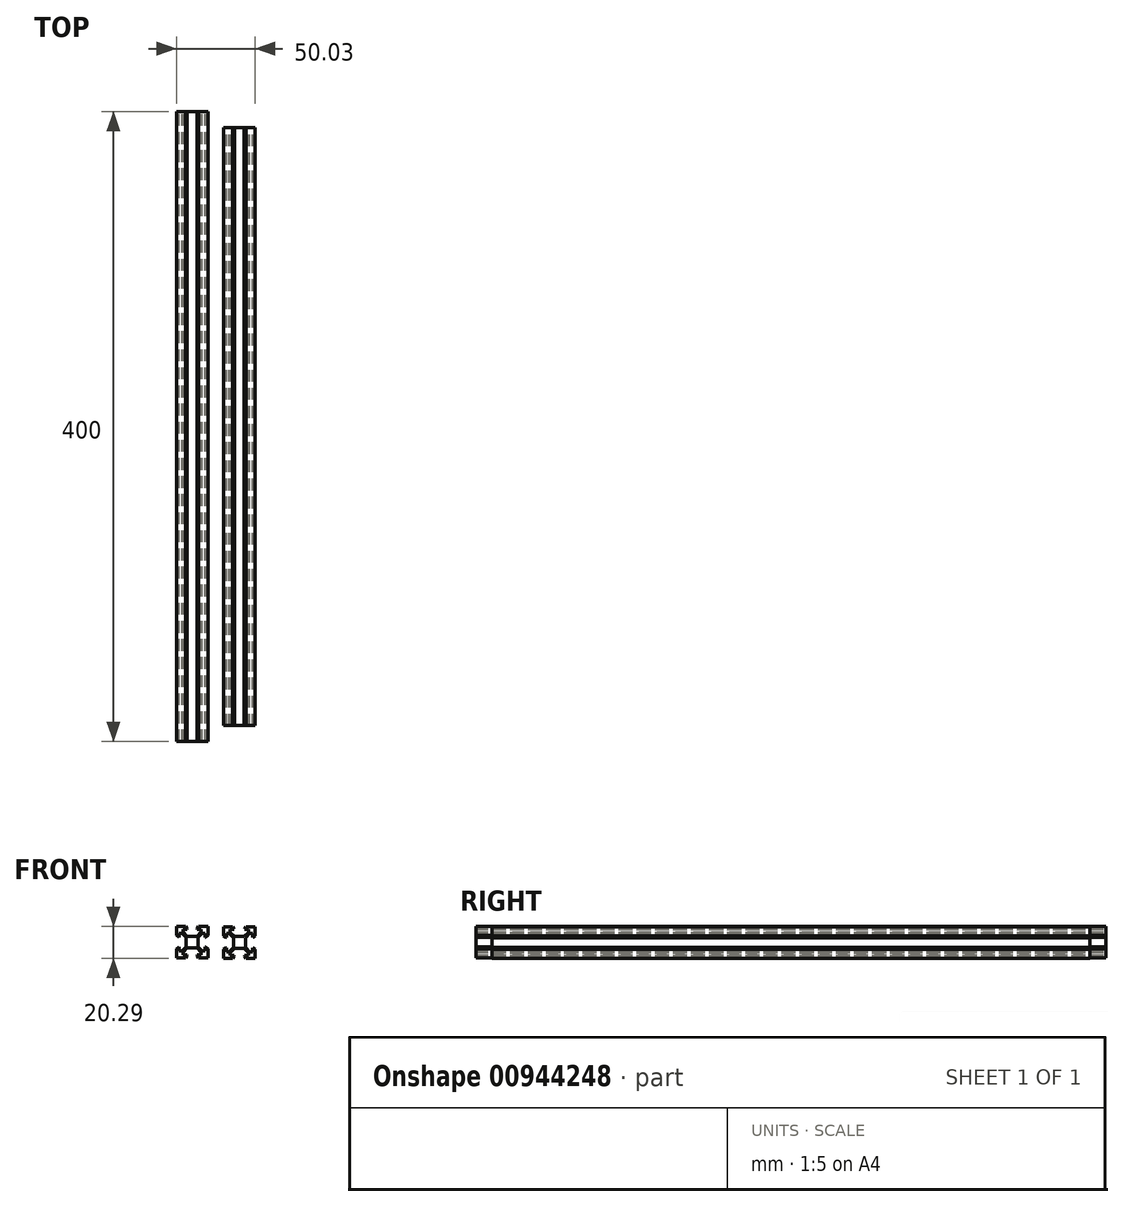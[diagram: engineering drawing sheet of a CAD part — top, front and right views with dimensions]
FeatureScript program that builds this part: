
annotation { "Feature Type Name" : "Feature", "Feature Type Description" : "" }
export const myFeature = defineFeature(function(context is Context, id is Id, definition is map)
    precondition{}
    {
        {
            var Q0;
            Q0=qCreatedBy(makeId("Front.planeOp"),FACE);
            var sketch = newSketch(context, id + "F0", { "sketchPlane" : qUnion([Q0])});
            skLineSegment(sketch, "E0.bottom", {"start": v(10, -10) * mm, "end": v(-10, -10) * mm});
            skLineSegment(sketch, "E0.top", {"start": v(10, 10) * mm, "end": v(-10, 10) * mm});
            skLineSegment(sketch, "E0.left", {"start": v(10, -10) * mm, "end": v(10, 10) * mm});
            skLineSegment(sketch, "E0.right", {"start": v(-10, -10) * mm, "end": v(-10, 10) * mm});
            skPoint(sketch, "E0.middle", {"position": v(0, 0) * mm});
            skLineSegment(sketch, "E1", {"start": v(4.24, 10) * mm, "end": v(3.26, 8.42) * mm});
            skLineSegment(sketch, "E2", {"start": v(3.26, 8.42) * mm, "end": v(3.26, 8.22) * mm});
            skLineSegment(sketch, "E3", {"start": v(3.26, 8.22) * mm, "end": v(5.76, 8.22) * mm});
            skLineSegment(sketch, "E4", {"start": v(5.76, 8.22) * mm, "end": v(5.76, 6.44) * mm});
            skLineSegment(sketch, "E5", {"start": v(5.76, 6.44) * mm, "end": v(3.11, 3.78) * mm});
            skLineSegment(sketch, "E6", {"start": v(3.11, 3.78) * mm, "end": v(0, 3.78) * mm});
            skLineSegment(sketch, "E7", {"start": v(0, 15.87) * mm, "end": v(0, -18.37) * mm, "construction": true});
            skPoint(sketch, "E7.endSnap0", {"position": v(0, -10) * mm});
            skLineSegment(sketch, "E8.MirrorCS", {"start": v(-4.24, 10) * mm, "end": v(-3.26, 8.42) * mm});
            skLineSegment(sketch, "E9.MirrorCS", {"start": v(-3.26, 8.42) * mm, "end": v(-3.26, 8.22) * mm});
            skLineSegment(sketch, "E10.MirrorCS", {"start": v(-3.26, 8.22) * mm, "end": v(-5.76, 8.22) * mm});
            skLineSegment(sketch, "E11.MirrorCS", {"start": v(-5.46, 15.87) * mm, "end": v(-5.46, -18.37) * mm, "construction": true});
            skLineSegment(sketch, "E12.MirrorCS", {"start": v(-5.76, 6.44) * mm, "end": v(-3.11, 3.78) * mm});
            skLineSegment(sketch, "E13.MirrorCS", {"start": v(-3.11, 3.78) * mm, "end": v(0, 3.78) * mm});
            skLineSegment(sketch, "E14.MirrorCS", {"start": v(-5.76, 8.22) * mm, "end": v(-5.76, 6.44) * mm});
            skLineSegment(sketch, "E15.1.0", {"start": v(-3.78, 3.11) * mm, "end": v(-3.78, 0) * mm});
            skLineSegment(sketch, "E15.1.1", {"start": v(-3.78, -3.11) * mm, "end": v(-3.78, 0) * mm});
            skLineSegment(sketch, "E15.1.2", {"start": v(-6.44, -5.76) * mm, "end": v(-3.78, -3.11) * mm});
            skLineSegment(sketch, "E15.1.3", {"start": v(-8.22, 3.26) * mm, "end": v(-8.22, 5.76) * mm});
            skLineSegment(sketch, "E15.1.4", {"start": v(-10, 4.24) * mm, "end": v(-8.42, 3.26) * mm});
            skLineSegment(sketch, "E15.1.5", {"start": v(-8.22, 5.76) * mm, "end": v(-6.44, 5.76) * mm});
            skLineSegment(sketch, "E15.1.6", {"start": v(-10, -4.24) * mm, "end": v(-8.42, -3.26) * mm});
            skLineSegment(sketch, "E15.1.7", {"start": v(-6.44, 5.76) * mm, "end": v(-3.78, 3.11) * mm});
            skLineSegment(sketch, "E15.1.8", {"start": v(-8.22, -5.76) * mm, "end": v(-6.44, -5.76) * mm});
            skLineSegment(sketch, "E15.1.9", {"start": v(-8.22, -3.26) * mm, "end": v(-8.22, -5.76) * mm});
            skLineSegment(sketch, "E15.1.10", {"start": v(-8.42, -3.26) * mm, "end": v(-8.22, -3.26) * mm});
            skLineSegment(sketch, "E15.1.11", {"start": v(-8.42, 3.26) * mm, "end": v(-8.22, 3.26) * mm});
            skLineSegment(sketch, "E15.2.0", {"start": v(-3.11, -3.78) * mm, "end": v(0, -3.78) * mm});
            skLineSegment(sketch, "E15.2.1", {"start": v(3.11, -3.78) * mm, "end": v(0, -3.78) * mm});
            skLineSegment(sketch, "E15.2.2", {"start": v(5.76, -6.44) * mm, "end": v(3.11, -3.78) * mm});
            skLineSegment(sketch, "E15.2.3", {"start": v(-3.26, -8.22) * mm, "end": v(-5.76, -8.22) * mm});
            skLineSegment(sketch, "E15.2.4", {"start": v(-4.24, -10) * mm, "end": v(-3.26, -8.42) * mm});
            skLineSegment(sketch, "E15.2.5", {"start": v(-5.76, -8.22) * mm, "end": v(-5.76, -6.44) * mm});
            skLineSegment(sketch, "E15.2.6", {"start": v(4.24, -10) * mm, "end": v(3.26, -8.42) * mm});
            skLineSegment(sketch, "E15.2.7", {"start": v(-5.76, -6.44) * mm, "end": v(-3.11, -3.78) * mm});
            skLineSegment(sketch, "E15.2.8", {"start": v(5.76, -8.22) * mm, "end": v(5.76, -6.44) * mm});
            skLineSegment(sketch, "E15.2.9", {"start": v(3.26, -8.22) * mm, "end": v(5.76, -8.22) * mm});
            skLineSegment(sketch, "E15.2.10", {"start": v(3.26, -8.42) * mm, "end": v(3.26, -8.22) * mm});
            skLineSegment(sketch, "E15.2.11", {"start": v(-3.26, -8.42) * mm, "end": v(-3.26, -8.22) * mm});
            skLineSegment(sketch, "E15.3.0", {"start": v(3.78, -3.11) * mm, "end": v(3.78, 0) * mm});
            skLineSegment(sketch, "E15.3.1", {"start": v(3.78, 3.11) * mm, "end": v(3.78, 0) * mm});
            skLineSegment(sketch, "E15.3.2", {"start": v(6.44, 5.76) * mm, "end": v(3.78, 3.11) * mm});
            skLineSegment(sketch, "E15.3.3", {"start": v(8.22, -3.26) * mm, "end": v(8.22, -5.76) * mm});
            skLineSegment(sketch, "E15.3.4", {"start": v(10, -4.24) * mm, "end": v(8.42, -3.26) * mm});
            skLineSegment(sketch, "E15.3.5", {"start": v(8.22, -5.76) * mm, "end": v(6.44, -5.76) * mm});
            skLineSegment(sketch, "E15.3.6", {"start": v(10, 4.24) * mm, "end": v(8.42, 3.26) * mm});
            skLineSegment(sketch, "E15.3.7", {"start": v(6.44, -5.76) * mm, "end": v(3.78, -3.11) * mm});
            skLineSegment(sketch, "E15.3.8", {"start": v(8.22, 5.76) * mm, "end": v(6.44, 5.76) * mm});
            skLineSegment(sketch, "E15.3.9", {"start": v(8.22, 3.26) * mm, "end": v(8.22, 5.76) * mm});
            skLineSegment(sketch, "E15.3.10", {"start": v(8.42, 3.26) * mm, "end": v(8.22, 3.26) * mm});
            skLineSegment(sketch, "E15.3.11", {"start": v(8.42, -3.26) * mm, "end": v(8.22, -3.26) * mm});
            skSolve(sketch);
        }
        {
            var Q0;
            {var subQ15=sQuery(id+"F0.wireOp",EDGE,"E1");Q0=makeQuery(id+"F0.imprint","IMPRINT",FACE,{"disambiguationData":[TD([[makeQuery(id+"F0.imprint","IMPRINT",EDGE,{"derivedFrom":subQ15}),1.0]])]});}
            extrude(context, id + "F1", {"entities" : qUnion([Q0]), "depth" : 380 * mm, "symmetric" : true});
        }
        {
            var Q0;
            Q0=makeQuery(id+"F1.opExtrude","SWEPT_BODY",BODY,{"disambiguationData":[OSD([sQuery(id+"F0.wireOp",EDGE,"E0.bottom"),sQuery(id+"F0.wireOp",EDGE,"E0.top"),sQuery(id+"F0.wireOp",EDGE,"E0.left"),sQuery(id+"F0.wireOp",EDGE,"E0.right"),sQuery(id+"F0.wireOp",EDGE,"E1"),sQuery(id+"F0.wireOp",EDGE,"E2"),sQuery(id+"F0.wireOp",EDGE,"E3"),sQuery(id+"F0.wireOp",EDGE,"E4"),sQuery(id+"F0.wireOp",EDGE,"E5"),sQuery(id+"F0.wireOp",EDGE,"E6"),sQuery(id+"F0.wireOp",EDGE,"E8.MirrorCS"),sQuery(id+"F0.wireOp",EDGE,"E9.MirrorCS"),sQuery(id+"F0.wireOp",EDGE,"E10.MirrorCS"),sQuery(id+"F0.wireOp",EDGE,"E12.MirrorCS"),sQuery(id+"F0.wireOp",EDGE,"E13.MirrorCS"),sQuery(id+"F0.wireOp",EDGE,"E14.MirrorCS"),sQuery(id+"F0.wireOp",EDGE,"E15.1.0"),sQuery(id+"F0.wireOp",EDGE,"E15.1.1"),sQuery(id+"F0.wireOp",EDGE,"E15.1.2"),sQuery(id+"F0.wireOp",EDGE,"E15.1.3"),sQuery(id+"F0.wireOp",EDGE,"E15.1.4"),sQuery(id+"F0.wireOp",EDGE,"E15.1.5"),sQuery(id+"F0.wireOp",EDGE,"E15.1.6"),sQuery(id+"F0.wireOp",EDGE,"E15.1.7"),sQuery(id+"F0.wireOp",EDGE,"E15.1.8"),sQuery(id+"F0.wireOp",EDGE,"E15.1.9"),sQuery(id+"F0.wireOp",EDGE,"E15.1.10"),sQuery(id+"F0.wireOp",EDGE,"E15.1.11"),sQuery(id+"F0.wireOp",EDGE,"E15.2.0"),sQuery(id+"F0.wireOp",EDGE,"E15.2.1"),sQuery(id+"F0.wireOp",EDGE,"E15.2.2"),sQuery(id+"F0.wireOp",EDGE,"E15.2.3"),sQuery(id+"F0.wireOp",EDGE,"E15.2.4"),sQuery(id+"F0.wireOp",EDGE,"E15.2.5"),sQuery(id+"F0.wireOp",EDGE,"E15.2.6"),sQuery(id+"F0.wireOp",EDGE,"E15.2.7"),sQuery(id+"F0.wireOp",EDGE,"E15.2.8"),sQuery(id+"F0.wireOp",EDGE,"E15.2.9"),sQuery(id+"F0.wireOp",EDGE,"E15.2.10"),sQuery(id+"F0.wireOp",EDGE,"E15.2.11"),sQuery(id+"F0.wireOp",EDGE,"E15.3.0"),sQuery(id+"F0.wireOp",EDGE,"E15.3.1"),sQuery(id+"F0.wireOp",EDGE,"E15.3.2"),sQuery(id+"F0.wireOp",EDGE,"E15.3.3"),sQuery(id+"F0.wireOp",EDGE,"E15.3.4"),sQuery(id+"F0.wireOp",EDGE,"E15.3.5"),sQuery(id+"F0.wireOp",EDGE,"E15.3.6"),sQuery(id+"F0.wireOp",EDGE,"E15.3.7"),sQuery(id+"F0.wireOp",EDGE,"E15.3.8"),sQuery(id+"F0.wireOp",EDGE,"E15.3.9"),sQuery(id+"F0.wireOp",EDGE,"E15.3.10"),sQuery(id+"F0.wireOp",EDGE,"E15.3.11")])]});
            transform(context, id + "F2", {"entities" : qUnion([Q0]), "transformType" : TransformType.COPY});
        }
        {
            var Q0;
            Q0=makeQuery(id+"F2.opPattern","COPY",BODY,{"derivedFrom":makeQuery(id+"F1.opExtrude","SWEPT_BODY",BODY,{"disambiguationData":[OSD([sQuery(id+"F0.wireOp",EDGE,"E0.bottom"),sQuery(id+"F0.wireOp",EDGE,"E0.top"),sQuery(id+"F0.wireOp",EDGE,"E0.left"),sQuery(id+"F0.wireOp",EDGE,"E0.right"),sQuery(id+"F0.wireOp",EDGE,"E1"),sQuery(id+"F0.wireOp",EDGE,"E2"),sQuery(id+"F0.wireOp",EDGE,"E3"),sQuery(id+"F0.wireOp",EDGE,"E4"),sQuery(id+"F0.wireOp",EDGE,"E5"),sQuery(id+"F0.wireOp",EDGE,"E6"),sQuery(id+"F0.wireOp",EDGE,"E8.MirrorCS"),sQuery(id+"F0.wireOp",EDGE,"E9.MirrorCS"),sQuery(id+"F0.wireOp",EDGE,"E10.MirrorCS"),sQuery(id+"F0.wireOp",EDGE,"E12.MirrorCS"),sQuery(id+"F0.wireOp",EDGE,"E13.MirrorCS"),sQuery(id+"F0.wireOp",EDGE,"E14.MirrorCS"),sQuery(id+"F0.wireOp",EDGE,"E15.1.0"),sQuery(id+"F0.wireOp",EDGE,"E15.1.1"),sQuery(id+"F0.wireOp",EDGE,"E15.1.2"),sQuery(id+"F0.wireOp",EDGE,"E15.1.3"),sQuery(id+"F0.wireOp",EDGE,"E15.1.4"),sQuery(id+"F0.wireOp",EDGE,"E15.1.5"),sQuery(id+"F0.wireOp",EDGE,"E15.1.6"),sQuery(id+"F0.wireOp",EDGE,"E15.1.7"),sQuery(id+"F0.wireOp",EDGE,"E15.1.8"),sQuery(id+"F0.wireOp",EDGE,"E15.1.9"),sQuery(id+"F0.wireOp",EDGE,"E15.1.10"),sQuery(id+"F0.wireOp",EDGE,"E15.1.11"),sQuery(id+"F0.wireOp",EDGE,"E15.2.0"),sQuery(id+"F0.wireOp",EDGE,"E15.2.1"),sQuery(id+"F0.wireOp",EDGE,"E15.2.2"),sQuery(id+"F0.wireOp",EDGE,"E15.2.3"),sQuery(id+"F0.wireOp",EDGE,"E15.2.4"),sQuery(id+"F0.wireOp",EDGE,"E15.2.5"),sQuery(id+"F0.wireOp",EDGE,"E15.2.6"),sQuery(id+"F0.wireOp",EDGE,"E15.2.7"),sQuery(id+"F0.wireOp",EDGE,"E15.2.8"),sQuery(id+"F0.wireOp",EDGE,"E15.2.9"),sQuery(id+"F0.wireOp",EDGE,"E15.2.10"),sQuery(id+"F0.wireOp",EDGE,"E15.2.11"),sQuery(id+"F0.wireOp",EDGE,"E15.3.0"),sQuery(id+"F0.wireOp",EDGE,"E15.3.1"),sQuery(id+"F0.wireOp",EDGE,"E15.3.2"),sQuery(id+"F0.wireOp",EDGE,"E15.3.3"),sQuery(id+"F0.wireOp",EDGE,"E15.3.4"),sQuery(id+"F0.wireOp",EDGE,"E15.3.5"),sQuery(id+"F0.wireOp",EDGE,"E15.3.6"),sQuery(id+"F0.wireOp",EDGE,"E15.3.7"),sQuery(id+"F0.wireOp",EDGE,"E15.3.8"),sQuery(id+"F0.wireOp",EDGE,"E15.3.9"),sQuery(id+"F0.wireOp",EDGE,"E15.3.10"),sQuery(id+"F0.wireOp",EDGE,"E15.3.11")])]}),"instanceName":"1"});
            deleteBodies(context, id + "F3", {"entities" : qUnion([Q0])});
        }
        {
            var Q0;
            Q0=makeQuery(id+"F1.opExtrude","SWEPT_BODY",BODY,{"disambiguationData":[OSD([sQuery(id+"F0.wireOp",EDGE,"E0.bottom"),sQuery(id+"F0.wireOp",EDGE,"E0.top"),sQuery(id+"F0.wireOp",EDGE,"E0.left"),sQuery(id+"F0.wireOp",EDGE,"E0.right"),sQuery(id+"F0.wireOp",EDGE,"E1"),sQuery(id+"F0.wireOp",EDGE,"E2"),sQuery(id+"F0.wireOp",EDGE,"E3"),sQuery(id+"F0.wireOp",EDGE,"E4"),sQuery(id+"F0.wireOp",EDGE,"E5"),sQuery(id+"F0.wireOp",EDGE,"E6"),sQuery(id+"F0.wireOp",EDGE,"E8.MirrorCS"),sQuery(id+"F0.wireOp",EDGE,"E9.MirrorCS"),sQuery(id+"F0.wireOp",EDGE,"E10.MirrorCS"),sQuery(id+"F0.wireOp",EDGE,"E12.MirrorCS"),sQuery(id+"F0.wireOp",EDGE,"E13.MirrorCS"),sQuery(id+"F0.wireOp",EDGE,"E14.MirrorCS"),sQuery(id+"F0.wireOp",EDGE,"E15.1.0"),sQuery(id+"F0.wireOp",EDGE,"E15.1.1"),sQuery(id+"F0.wireOp",EDGE,"E15.1.2"),sQuery(id+"F0.wireOp",EDGE,"E15.1.3"),sQuery(id+"F0.wireOp",EDGE,"E15.1.4"),sQuery(id+"F0.wireOp",EDGE,"E15.1.5"),sQuery(id+"F0.wireOp",EDGE,"E15.1.6"),sQuery(id+"F0.wireOp",EDGE,"E15.1.7"),sQuery(id+"F0.wireOp",EDGE,"E15.1.8"),sQuery(id+"F0.wireOp",EDGE,"E15.1.9"),sQuery(id+"F0.wireOp",EDGE,"E15.1.10"),sQuery(id+"F0.wireOp",EDGE,"E15.1.11"),sQuery(id+"F0.wireOp",EDGE,"E15.2.0"),sQuery(id+"F0.wireOp",EDGE,"E15.2.1"),sQuery(id+"F0.wireOp",EDGE,"E15.2.2"),sQuery(id+"F0.wireOp",EDGE,"E15.2.3"),sQuery(id+"F0.wireOp",EDGE,"E15.2.4"),sQuery(id+"F0.wireOp",EDGE,"E15.2.5"),sQuery(id+"F0.wireOp",EDGE,"E15.2.6"),sQuery(id+"F0.wireOp",EDGE,"E15.2.7"),sQuery(id+"F0.wireOp",EDGE,"E15.2.8"),sQuery(id+"F0.wireOp",EDGE,"E15.2.9"),sQuery(id+"F0.wireOp",EDGE,"E15.2.10"),sQuery(id+"F0.wireOp",EDGE,"E15.2.11"),sQuery(id+"F0.wireOp",EDGE,"E15.3.0"),sQuery(id+"F0.wireOp",EDGE,"E15.3.1"),sQuery(id+"F0.wireOp",EDGE,"E15.3.2"),sQuery(id+"F0.wireOp",EDGE,"E15.3.3"),sQuery(id+"F0.wireOp",EDGE,"E15.3.4"),sQuery(id+"F0.wireOp",EDGE,"E15.3.5"),sQuery(id+"F0.wireOp",EDGE,"E15.3.6"),sQuery(id+"F0.wireOp",EDGE,"E15.3.7"),sQuery(id+"F0.wireOp",EDGE,"E15.3.8"),sQuery(id+"F0.wireOp",EDGE,"E15.3.9"),sQuery(id+"F0.wireOp",EDGE,"E15.3.10"),sQuery(id+"F0.wireOp",EDGE,"E15.3.11")])]});
            transform(context, id + "F4", {"entities" : qUnion([Q0]), "transformType" : TransformType.TRANSLATION_3D, "dx" : 30.3 * mm, "dy" : 0 * mm, "dz" : 0 * mm, "makeCopy" : false});
        }
        {
            var Q0;
            Q0=qCreatedBy(makeId("Front.planeOp"),FACE);
            var sketch = newSketch(context, id + "F5", { "sketchPlane" : qUnion([Q0])});
            skLineSegment(sketch, "E16.bottom", {"start": v(10.27, -9.71) * mm, "end": v(-9.73, -9.71) * mm});
            skLineSegment(sketch, "E16.top", {"start": v(10.27, 10.29) * mm, "end": v(-9.73, 10.29) * mm});
            skLineSegment(sketch, "E16.left", {"start": v(10.27, -9.71) * mm, "end": v(10.27, 10.29) * mm});
            skLineSegment(sketch, "E16.right", {"start": v(-9.73, -9.71) * mm, "end": v(-9.73, 10.29) * mm});
            skPoint(sketch, "E16.middle", {"position": v(0.27, 0.29) * mm});
            skLineSegment(sketch, "E17", {"start": v(4.51, 10.29) * mm, "end": v(3.38, 8.71) * mm});
            skLineSegment(sketch, "E18", {"start": v(3.38, 8.71) * mm, "end": v(3.38, 8.5) * mm});
            skLineSegment(sketch, "E19", {"start": v(3.38, 8.5) * mm, "end": v(5.88, 8.5) * mm});
            skLineSegment(sketch, "E20", {"start": v(5.88, 8.5) * mm, "end": v(5.88, 6.73) * mm});
            skLineSegment(sketch, "E21", {"start": v(5.88, 6.73) * mm, "end": v(3.38, 4.06) * mm});
            skLineSegment(sketch, "E22", {"start": v(3.38, 4.06) * mm, "end": v(0.27, 4.06) * mm});
            skLineSegment(sketch, "E23", {"start": v(0.27, 16.16) * mm, "end": v(0.27, -18.08) * mm, "construction": true});
            skPoint(sketch, "E23.endSnap0", {"position": v(0.27, -9.71) * mm});
            skLineSegment(sketch, "E24.MirrorCS", {"start": v(-3.98, 10.29) * mm, "end": v(-2.84, 8.71) * mm});
            skLineSegment(sketch, "E25.MirrorCS", {"start": v(-2.84, 8.71) * mm, "end": v(-2.84, 8.5) * mm});
            skLineSegment(sketch, "E26.MirrorCS", {"start": v(-2.84, 8.5) * mm, "end": v(-5.34, 8.5) * mm});
            skLineSegment(sketch, "E27.MirrorCS", {"start": v(-5.2, 16.16) * mm, "end": v(-5.2, -18.08) * mm, "construction": true});
            skLineSegment(sketch, "E28.MirrorCS", {"start": v(-5.34, 6.73) * mm, "end": v(-2.84, 4.06) * mm});
            skLineSegment(sketch, "E29.MirrorCS", {"start": v(-2.84, 4.06) * mm, "end": v(0.27, 4.06) * mm});
            skLineSegment(sketch, "E30.MirrorCS", {"start": v(-5.34, 8.5) * mm, "end": v(-5.34, 6.73) * mm});
            skLineSegment(sketch, "E31.1.0", {"start": v(-3.5, 3.4) * mm, "end": v(-3.5, 0.29) * mm});
            skLineSegment(sketch, "E31.1.1", {"start": v(-3.5, -2.82) * mm, "end": v(-3.5, 0.29) * mm});
            skLineSegment(sketch, "E31.1.2", {"start": v(-6.18, -5.32) * mm, "end": v(-3.5, -2.82) * mm});
            skLineSegment(sketch, "E31.1.3", {"start": v(-7.95, 3.4) * mm, "end": v(-7.95, 5.9) * mm});
            skLineSegment(sketch, "E31.1.4", {"start": v(-9.73, 4.53) * mm, "end": v(-8.16, 3.4) * mm});
            skLineSegment(sketch, "E31.1.5", {"start": v(-7.95, 5.9) * mm, "end": v(-6.18, 5.9) * mm});
            skLineSegment(sketch, "E31.1.6", {"start": v(-9.73, -3.96) * mm, "end": v(-8.16, -2.82) * mm});
            skLineSegment(sketch, "E31.1.7", {"start": v(-6.18, 5.9) * mm, "end": v(-3.5, 3.4) * mm});
            skLineSegment(sketch, "E31.1.8", {"start": v(-7.95, -5.32) * mm, "end": v(-6.18, -5.32) * mm});
            skLineSegment(sketch, "E31.1.9", {"start": v(-7.95, -2.82) * mm, "end": v(-7.95, -5.32) * mm});
            skLineSegment(sketch, "E31.1.10", {"start": v(-8.16, -2.82) * mm, "end": v(-7.95, -2.82) * mm});
            skLineSegment(sketch, "E31.1.11", {"start": v(-8.16, 3.4) * mm, "end": v(-7.95, 3.4) * mm});
            skLineSegment(sketch, "E31.2.0", {"start": v(-2.84, -3.5) * mm, "end": v(0.27, -3.5) * mm});
            skLineSegment(sketch, "E31.2.1", {"start": v(3.38, -3.5) * mm, "end": v(0.27, -3.5) * mm});
            skLineSegment(sketch, "E31.2.2", {"start": v(5.88, -6.16) * mm, "end": v(3.38, -3.5) * mm});
            skLineSegment(sketch, "E31.2.3", {"start": v(-2.84, -7.94) * mm, "end": v(-5.34, -7.94) * mm});
            skLineSegment(sketch, "E31.2.4", {"start": v(-3.98, -9.71) * mm, "end": v(-2.84, -8.14) * mm});
            skLineSegment(sketch, "E31.2.5", {"start": v(-5.34, -7.94) * mm, "end": v(-5.34, -6.16) * mm});
            skLineSegment(sketch, "E31.2.6", {"start": v(4.51, -9.71) * mm, "end": v(3.38, -8.14) * mm});
            skLineSegment(sketch, "E31.2.7", {"start": v(-5.34, -6.16) * mm, "end": v(-2.84, -3.5) * mm});
            skLineSegment(sketch, "E31.2.8", {"start": v(5.88, -7.94) * mm, "end": v(5.88, -6.16) * mm});
            skLineSegment(sketch, "E31.2.9", {"start": v(3.38, -7.94) * mm, "end": v(5.88, -7.94) * mm});
            skLineSegment(sketch, "E31.2.10", {"start": v(3.38, -8.14) * mm, "end": v(3.38, -7.94) * mm});
            skLineSegment(sketch, "E31.2.11", {"start": v(-2.84, -8.14) * mm, "end": v(-2.84, -7.94) * mm});
            skLineSegment(sketch, "E31.3.0", {"start": v(4.05, -2.82) * mm, "end": v(4.05, 0.29) * mm});
            skLineSegment(sketch, "E31.3.1", {"start": v(4.05, 3.4) * mm, "end": v(4.05, 0.29) * mm});
            skLineSegment(sketch, "E31.3.2", {"start": v(6.71, 5.9) * mm, "end": v(4.05, 3.4) * mm});
            skLineSegment(sketch, "E31.3.3", {"start": v(8.5, -2.82) * mm, "end": v(8.5, -5.32) * mm});
            skLineSegment(sketch, "E31.3.4", {"start": v(10.27, -3.96) * mm, "end": v(8.7, -2.82) * mm});
            skLineSegment(sketch, "E31.3.5", {"start": v(8.5, -5.32) * mm, "end": v(6.71, -5.32) * mm});
            skLineSegment(sketch, "E31.3.6", {"start": v(10.27, 4.53) * mm, "end": v(8.7, 3.4) * mm});
            skLineSegment(sketch, "E31.3.7", {"start": v(6.71, -5.32) * mm, "end": v(4.05, -2.82) * mm});
            skLineSegment(sketch, "E31.3.8", {"start": v(8.5, 5.9) * mm, "end": v(6.71, 5.9) * mm});
            skLineSegment(sketch, "E31.3.9", {"start": v(8.5, 3.4) * mm, "end": v(8.5, 5.9) * mm});
            skLineSegment(sketch, "E31.3.10", {"start": v(8.7, 3.4) * mm, "end": v(8.5, 3.4) * mm});
            skLineSegment(sketch, "E31.3.11", {"start": v(8.7, -2.82) * mm, "end": v(8.5, -2.82) * mm});
            skSolve(sketch);
        }
        {
            var Q0;
            {var subQ11=sQuery(id+"F5.wireOp",EDGE,"E17");Q0=makeQuery(id+"F5.imprint","IMPRINT",FACE,{"disambiguationData":[TD([[makeQuery(id+"F5.imprint","IMPRINT",EDGE,{"derivedFrom":subQ11}),1.0]])]});}
            extrude(context, id + "F6", {"entities" : qUnion([Q0]), "depth" : 400 * mm, "symmetric" : true});
        }
    });
